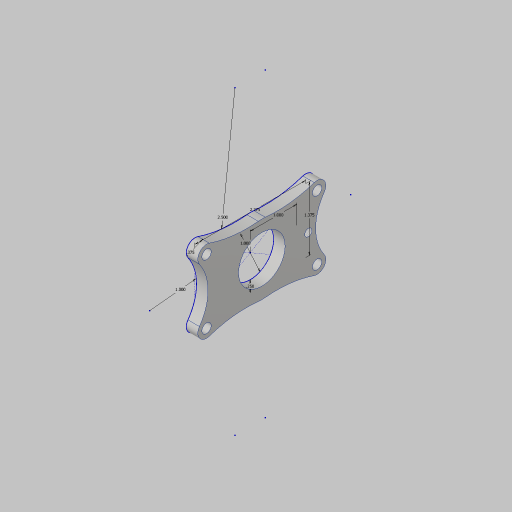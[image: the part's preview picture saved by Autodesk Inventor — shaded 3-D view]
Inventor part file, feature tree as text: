
AUTODESK INVENTOR PART (.ipt)
format: ipt  version: 2023.5 (Build 275446000, 446)  size: 135,680 bytes
history: native  units: in
note: dims shown in document units (in); Inventor stores cm internally (conversion verified against a paired STEP export)
features: hole x2, sketch x1, extrude x1
ambient origin geometry x8: Origin, YZ Plane, XZ Plane, XY Plane, X Axis, Y Axis, Z Axis, Center Point
bodies: Solid1 (feature_tree)
feature tree (4):
  sketch  "Sketch1"  dims[d1=1.375in d2=2.375in d3=1.0in d4=0.375in d5=1.0in d6=0.25in d7=2.5in d8=1.0in d9=0.25in d10=0.0in d11=0.201in d12=0.75in d13=0.385in d14=0.25in d15=0.5635in d16=1.0in d17=0.8108in d18=0.156in d19=0.38in d20=0.375in d21=0.25in d22=0.5635in d23=1.0in d24=0.8108in]
  extrude  "Extrusion1"  Depth=1.0in
  hole  "Hole1"  [1 undecoded]
  hole  "Hole2"  [1 undecoded]
note: 2 required parameter values undecoded (feature->parameter linkage not recoverable at this tier; creation-order binding heuristic only, values carry confidence <= 0.55)
